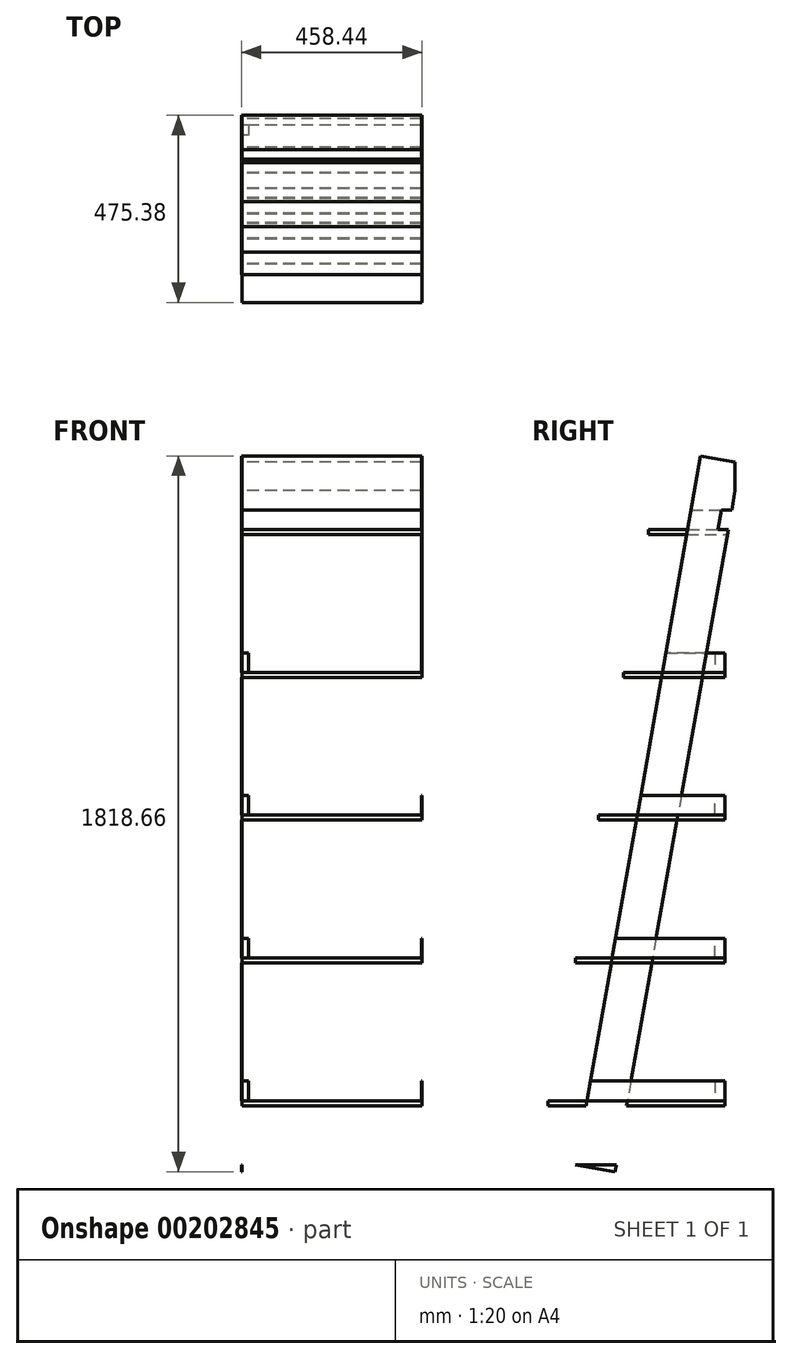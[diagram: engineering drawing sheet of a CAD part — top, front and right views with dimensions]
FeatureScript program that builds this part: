
annotation { "Feature Type Name" : "Feature", "Feature Type Description" : "" }
export const myFeature = defineFeature(function(context is Context, id is Id, definition is map)
    precondition{}
    {
        {
            assignVariable(context, id + "F0", {"name" : "Thickness", "anyValue" : 1.25});
        }
        {
            var Q0;
            Q0=qCreatedBy(makeId("Right.planeOp"),FACE);
            var sketch = newSketch(context, id + "F1", { "sketchPlane" : qUnion([Q0])});
            skLineSegment(sketch, "E0.bottom", {"start": v(317.57, 1801.02) * mm, "end": v(405.12, 1785.58) * mm});
            skLineSegment(sketch, "E0.top", {"start": v(0, 0) * mm, "end": v(100.06, -17.64) * mm});
            skLineSegment(sketch, "E0.left", {"start": v(317.57, 1801.02) * mm, "end": v(0, 0) * mm});
            skLineSegment(sketch, "E0.right", {"start": v(417.62, 1783.37) * mm, "end": v(405.12, 1712.44) * mm, "construction": true});
            skLineSegment(sketch, "E1", {"start": v(405.12, 1712.44) * mm, "end": v(405.12, 1785.58) * mm});
            skLineSegment(sketch, "E2", {"start": v(103.17, 0) * mm, "end": v(0, 0) * mm});
            skLineSegment(sketch, "E3.bottom", {"start": v(26.46, 150.08) * mm, "end": v(129.63, 150.08) * mm});
            skLineSegment(sketch, "E3.top", {"start": v(0, 0) * mm, "end": v(103.17, 0) * mm});
            skLineSegment(sketch, "E3.left", {"start": v(26.46, 150.08) * mm, "end": v(0, 0) * mm});
            skLineSegment(sketch, "E3.right", {"start": v(129.63, 150.08) * mm, "end": v(103.17, 0) * mm});
            skLineSegment(sketch, "E4.bottom", {"start": v(37.5, 212.62) * mm, "end": v(140.66, 212.62) * mm});
            skLineSegment(sketch, "E4.left", {"start": v(37.5, 212.62) * mm, "end": v(26.46, 150.08) * mm});
            skLineSegment(sketch, "E4.right", {"start": v(140.66, 212.62) * mm, "end": v(129.63, 150.08) * mm});
            skLineSegment(sketch, "E5", {"start": v(0, 0) * mm, "end": v(-478.22, 0) * mm, "construction": true});
            skLineSegment(sketch, "E6.0.1.0", {"start": v(204.61, 575.32) * mm, "end": v(193.59, 512.79) * mm});
            skLineSegment(sketch, "E6.0.1.1", {"start": v(101.45, 575.32) * mm, "end": v(204.61, 575.32) * mm});
            skLineSegment(sketch, "E6.0.1.2", {"start": v(101.45, 575.32) * mm, "end": v(90.42, 512.79) * mm});
            skLineSegment(sketch, "E6.0.1.3", {"start": v(90.42, 512.79) * mm, "end": v(193.59, 512.79) * mm});
            skLineSegment(sketch, "E6.0.2.0", {"start": v(268.57, 938.03) * mm, "end": v(257.54, 875.5) * mm});
            skLineSegment(sketch, "E6.0.2.1", {"start": v(165.4, 938.03) * mm, "end": v(268.57, 938.03) * mm});
            skLineSegment(sketch, "E6.0.2.2", {"start": v(165.4, 938.03) * mm, "end": v(154.37, 875.5) * mm});
            skLineSegment(sketch, "E6.0.2.3", {"start": v(154.37, 875.5) * mm, "end": v(257.54, 875.5) * mm});
            skLineSegment(sketch, "E6.0.3.0", {"start": v(332.52, 1300.73) * mm, "end": v(321.5, 1238.2) * mm});
            skLineSegment(sketch, "E6.0.3.1", {"start": v(229.35, 1300.73) * mm, "end": v(332.52, 1300.73) * mm});
            skLineSegment(sketch, "E6.0.3.2", {"start": v(229.35, 1300.73) * mm, "end": v(218.33, 1238.2) * mm});
            skLineSegment(sketch, "E6.0.3.3", {"start": v(218.33, 1238.2) * mm, "end": v(321.5, 1238.2) * mm});
            skLineSegment(sketch, "E6.direction1", {"start": v(129.63, 150.08) * mm, "end": v(405.12, 150.08) * mm, "construction": true});
            skLineSegment(sketch, "E6.direction2", {"start": v(129.63, 150.08) * mm, "end": v(193.59, 512.79) * mm, "construction": true});
            skLineSegment(sketch, "E7.0.0.4", {"start": v(396.48, 1663.44) * mm, "end": v(385.45, 1600.9) * mm});
            skLineSegment(sketch, "E7.3.0.4", {"start": v(293.3, 1663.44) * mm, "end": v(396.48, 1663.44) * mm});
            skLineSegment(sketch, "E7.6.0.4", {"start": v(293.3, 1663.44) * mm, "end": v(282.28, 1600.9) * mm});
            skLineSegment(sketch, "E7.9.0.4", {"start": v(282.28, 1600.9) * mm, "end": v(385.45, 1600.9) * mm});
            skLineSegment(sketch, "E8", {"start": v(405.12, 1785.58) * mm, "end": v(417.62, 1783.37) * mm, "construction": true});
            skLineSegment(sketch, "E9", {"start": v(405.12, 1712.44) * mm, "end": v(100.06, -17.64) * mm});
            skLineSegment(sketch, "E10", {"start": v(405.12, 2231.58) * mm, "end": v(405.12, 0) * mm, "construction": true});
            skPoint(sketch, "E11.firstSnap0", {"position": v(267.37, 150.08) * mm});
            skLineSegment(sketch, "E11.bottom", {"start": v(-70.26, 150.08) * mm, "end": v(379.72, 150.08) * mm});
            skLineSegment(sketch, "E11.top", {"start": v(-70.26, 162.78) * mm, "end": v(379.72, 162.78) * mm});
            skLineSegment(sketch, "E11.left", {"start": v(-70.26, 150.08) * mm, "end": v(-70.26, 162.78) * mm});
            skLineSegment(sketch, "E11.right", {"start": v(379.72, 150.08) * mm, "end": v(379.72, 162.78) * mm});
            skLineSegment(sketch, "E12.bottom", {"start": v(185.56, 1613.6) * mm, "end": v(387.69, 1613.6) * mm});
            skLineSegment(sketch, "E12.top", {"start": v(185.56, 1600.9) * mm, "end": v(387.69, 1600.9) * mm});
            skLineSegment(sketch, "E12.left", {"start": v(185.56, 1613.6) * mm, "end": v(185.56, 1600.9) * mm});
            skLineSegment(sketch, "E12.right", {"start": v(387.69, 1613.6) * mm, "end": v(387.69, 1600.9) * mm});
            skLineSegment(sketch, "E13.bottom", {"start": v(379.72, 1250.9) * mm, "end": v(121.6, 1250.9) * mm});
            skLineSegment(sketch, "E13.top", {"start": v(379.72, 1238.2) * mm, "end": v(121.6, 1238.2) * mm});
            skLineSegment(sketch, "E13.left", {"start": v(379.72, 1250.9) * mm, "end": v(379.72, 1238.2) * mm});
            skLineSegment(sketch, "E13.right", {"start": v(121.6, 1250.9) * mm, "end": v(121.6, 1238.2) * mm});
            skLineSegment(sketch, "E14.bottom", {"start": v(379.72, 888.2) * mm, "end": v(57.65, 888.2) * mm});
            skLineSegment(sketch, "E14.top", {"start": v(379.72, 875.5) * mm, "end": v(57.65, 875.5) * mm});
            skLineSegment(sketch, "E14.left", {"start": v(379.72, 888.2) * mm, "end": v(379.72, 875.5) * mm});
            skLineSegment(sketch, "E14.right", {"start": v(57.65, 888.2) * mm, "end": v(57.65, 875.5) * mm});
            skLineSegment(sketch, "E15.bottom", {"start": v(379.72, 512.79) * mm, "end": v(0, 512.79) * mm});
            skLineSegment(sketch, "E15.top", {"start": v(379.72, 525.49) * mm, "end": v(0, 525.49) * mm});
            skLineSegment(sketch, "E15.left", {"start": v(379.72, 525.49) * mm, "end": v(379.72, 512.79) * mm});
            skLineSegment(sketch, "E15.right", {"start": v(0, 525.49) * mm, "end": v(0, 512.79) * mm});
            skLineSegment(sketch, "E16", {"start": v(247.42, 1951.7) * mm, "end": v(-87, 55.12) * mm, "construction": true});
            skLineSegment(sketch, "E17", {"start": v(396.48, 1663.44) * mm, "end": v(387.69, 1613.6) * mm});
            skLineSegment(sketch, "E18", {"start": v(361.9, 1613.6) * mm, "end": v(370.68, 1663.44) * mm});
            skLineSegment(sketch, "E19", {"start": v(379.72, 1250.9) * mm, "end": v(379.72, 1300.73) * mm});
            skLineSegment(sketch, "E20", {"start": v(379.72, 1300.73) * mm, "end": v(332.52, 1300.73) * mm});
            skLineSegment(sketch, "E21", {"start": v(354.32, 1300.73) * mm, "end": v(354.32, 1250.9) * mm});
            skLineSegment(sketch, "E22", {"start": v(379.72, 888.2) * mm, "end": v(379.72, 938.03) * mm});
            skLineSegment(sketch, "E23", {"start": v(379.72, 938.03) * mm, "end": v(268.57, 938.03) * mm});
            skLineSegment(sketch, "E24", {"start": v(379.72, 525.49) * mm, "end": v(379.72, 575.32) * mm});
            skLineSegment(sketch, "E25", {"start": v(379.72, 575.32) * mm, "end": v(204.61, 575.32) * mm});
            skLineSegment(sketch, "E26", {"start": v(379.72, 162.78) * mm, "end": v(379.72, 212.62) * mm});
            skLineSegment(sketch, "E27", {"start": v(379.72, 212.62) * mm, "end": v(140.66, 212.62) * mm});
            skLineSegment(sketch, "E28", {"start": v(354.32, 212.62) * mm, "end": v(354.32, 162.78) * mm});
            skLineSegment(sketch, "E29", {"start": v(354.32, 525.49) * mm, "end": v(354.32, 575.32) * mm});
            skLineSegment(sketch, "E30", {"start": v(354.32, 888.2) * mm, "end": v(354.32, 938.03) * mm});
            skSolve(sketch);
        }
        {
            var Q0;
            {var subQ4=sQuery(id+"F1.wireOp",EDGE,"E0.bottom");Q0=makeQuery(id+"F1.imprint","IMPRINT",FACE,{"disambiguationData":[TD([[makeQuery(id+"F1.imprint","IMPRINT",EDGE,{"derivedFrom":subQ4}),-1.0]])]});}
            var Q1;
            {var subQ0=sQuery(id+"F1.wireOp",EDGE,"E17");Q1=makeQuery(id+"F1.imprint","IMPRINT",FACE,{"disambiguationData":[TD([[makeQuery(id+"F1.imprint","IMPRINT",EDGE,{"derivedFrom":subQ0}),-1.0]])]});}
            var Q2;
            {var subQ3=sQuery(id+"F1.wireOp",EDGE,"E18");Q2=makeQuery(id+"F1.imprint","IMPRINT",FACE,{"disambiguationData":[TD([[makeQuery(id+"F1.imprint","IMPRINT",EDGE,{"derivedFrom":subQ3}),1.0]])]});}
            var Q3;
            {var subQ0=sQuery(id+"F1.wireOp",EDGE,"E12.bottom");var subQ3=makeQuery(id+"F1.imprint","INTERSECT",VERTEX,{"derivedFrom":[subQ0,sQuery(id+"F1.wireOp",EDGE,"E18")]});Q3=makeQuery(id+"F1.imprint","IMPRINT",FACE,{"disambiguationData":[TD([[makeQuery(id+"F1.imprint","IMPRINT",EDGE,{"disambiguationData":[TD([[subQ3,1.0]])],"derivedFrom":subQ0}),-1.0]])]});}
            var Q4;
            {var subQ0=sQuery(id+"F1.wireOp",EDGE,"E6.0.3.1");Q4=makeQuery(id+"F1.imprint","IMPRINT",FACE,{"disambiguationData":[TD([[makeQuery(id+"F1.imprint","IMPRINT",EDGE,{"derivedFrom":subQ0}),1.0]])]});}
            var Q5;
            {var subQ0=sQuery(id+"F1.wireOp",EDGE,"E6.0.3.1");Q5=makeQuery(id+"F1.imprint","IMPRINT",FACE,{"disambiguationData":[TD([[makeQuery(id+"F1.imprint","IMPRINT",EDGE,{"derivedFrom":subQ0}),-1.0]])]});}
            var Q6;
            {var subQ0=sQuery(id+"F1.wireOp",EDGE,"E13.top");var subQ5=sQuery(id+"F1.wireOp",EDGE,"E9");var subQ6=makeQuery(id+"F1.imprint","INTERSECT",VERTEX,{"derivedFrom":[subQ5,subQ0]});Q6=makeQuery(id+"F1.imprint","IMPRINT",FACE,{"disambiguationData":[TD([[makeQuery(id+"F1.imprint","IMPRINT",EDGE,{"disambiguationData":[TD([[subQ6,1.0]])],"derivedFrom":subQ5}),-1.0]])]});}
            var Q7;
            {var subQ0=sQuery(id+"F1.wireOp",EDGE,"E6.0.2.1");Q7=makeQuery(id+"F1.imprint","IMPRINT",FACE,{"disambiguationData":[TD([[makeQuery(id+"F1.imprint","IMPRINT",EDGE,{"derivedFrom":subQ0}),1.0]])]});}
            var Q8;
            {var subQ0=sQuery(id+"F1.wireOp",EDGE,"E6.0.2.1");Q8=makeQuery(id+"F1.imprint","IMPRINT",FACE,{"disambiguationData":[TD([[makeQuery(id+"F1.imprint","IMPRINT",EDGE,{"derivedFrom":subQ0}),-1.0]])]});}
            var Q9;
            {var subQ0=sQuery(id+"F1.wireOp",EDGE,"E6.0.1.1");Q9=makeQuery(id+"F1.imprint","IMPRINT",FACE,{"disambiguationData":[TD([[makeQuery(id+"F1.imprint","IMPRINT",EDGE,{"derivedFrom":subQ0}),1.0]])]});}
            var Q10;
            {var subQ0=sQuery(id+"F1.wireOp",EDGE,"E14.top");var subQ5=sQuery(id+"F1.wireOp",EDGE,"E9");var subQ6=makeQuery(id+"F1.imprint","INTERSECT",VERTEX,{"derivedFrom":[subQ5,subQ0]});Q10=makeQuery(id+"F1.imprint","IMPRINT",FACE,{"disambiguationData":[TD([[makeQuery(id+"F1.imprint","IMPRINT",EDGE,{"disambiguationData":[TD([[subQ6,1.0]])],"derivedFrom":subQ5}),-1.0]])]});}
            var Q11;
            {var subQ0=sQuery(id+"F1.wireOp",EDGE,"E6.0.1.1");Q11=makeQuery(id+"F1.imprint","IMPRINT",FACE,{"disambiguationData":[TD([[makeQuery(id+"F1.imprint","IMPRINT",EDGE,{"derivedFrom":subQ0}),-1.0]])]});}
            var Q12;
            {var subQ0=sQuery(id+"F1.wireOp",EDGE,"E15.bottom");var subQ5=sQuery(id+"F1.wireOp",EDGE,"E9");var subQ6=makeQuery(id+"F1.imprint","INTERSECT",VERTEX,{"derivedFrom":[subQ5,subQ0]});Q12=makeQuery(id+"F1.imprint","IMPRINT",FACE,{"disambiguationData":[TD([[makeQuery(id+"F1.imprint","IMPRINT",EDGE,{"disambiguationData":[TD([[subQ6,1.0]])],"derivedFrom":subQ5}),-1.0]])]});}
            var Q13;
            {var subQ0=sQuery(id+"F1.wireOp",EDGE,"E4.bottom");Q13=makeQuery(id+"F1.imprint","IMPRINT",FACE,{"disambiguationData":[TD([[makeQuery(id+"F1.imprint","IMPRINT",EDGE,{"derivedFrom":subQ0}),1.0]])]});}
            var Q14;
            {var subQ0=sQuery(id+"F1.wireOp",EDGE,"E4.bottom");Q14=makeQuery(id+"F1.imprint","IMPRINT",FACE,{"disambiguationData":[TD([[makeQuery(id+"F1.imprint","IMPRINT",EDGE,{"derivedFrom":subQ0}),-1.0]])]});}
            var Q15;
            {var subQ0=sQuery(id+"F1.wireOp",EDGE,"E11.bottom");var subQ5=sQuery(id+"F1.wireOp",EDGE,"E9");var subQ6=makeQuery(id+"F1.imprint","INTERSECT",VERTEX,{"derivedFrom":[subQ5,subQ0]});Q15=makeQuery(id+"F1.imprint","IMPRINT",FACE,{"disambiguationData":[TD([[makeQuery(id+"F1.imprint","IMPRINT",EDGE,{"disambiguationData":[TD([[subQ6,1.0]])],"derivedFrom":subQ5}),-1.0]])]});}
            var Q16;
            {var subQ0=sQuery(id+"F1.wireOp",EDGE,"E3.top");Q16=makeQuery(id+"F1.imprint","IMPRINT",FACE,{"disambiguationData":[TD([[makeQuery(id+"F1.imprint","IMPRINT",EDGE,{"derivedFrom":subQ0}),1.0]])]});}
            extrude(context, id + "F2", {"entities" : qUnion([Q0, Q1, Q2, Q3, Q4, Q5, Q6, Q7, Q8, Q9, Q10, Q11, Q12, Q13, Q14, Q15, Q16]), "oppositeDirection" : true, "depth" : (getVariable(context, 'Thickness') / 2) * mm});
        }
        {
            var Q0;
            {var subQ4=sQuery(id+"F1.wireOp",EDGE,"E0.bottom");Q0=makeQuery(id+"F1.imprint","IMPRINT",FACE,{"disambiguationData":[TD([[makeQuery(id+"F1.imprint","IMPRINT",EDGE,{"derivedFrom":subQ4}),-1.0]])]});}
            var Q1;
            {var subQ0=sQuery(id+"F1.wireOp",EDGE,"E6.0.3.1");Q1=makeQuery(id+"F1.imprint","IMPRINT",FACE,{"disambiguationData":[TD([[makeQuery(id+"F1.imprint","IMPRINT",EDGE,{"derivedFrom":subQ0}),1.0]])]});}
            var Q2;
            {var subQ0=sQuery(id+"F1.wireOp",EDGE,"E6.0.2.1");Q2=makeQuery(id+"F1.imprint","IMPRINT",FACE,{"disambiguationData":[TD([[makeQuery(id+"F1.imprint","IMPRINT",EDGE,{"derivedFrom":subQ0}),1.0]])]});}
            var Q3;
            {var subQ0=sQuery(id+"F1.wireOp",EDGE,"E6.0.1.1");Q3=makeQuery(id+"F1.imprint","IMPRINT",FACE,{"disambiguationData":[TD([[makeQuery(id+"F1.imprint","IMPRINT",EDGE,{"derivedFrom":subQ0}),1.0]])]});}
            var Q4;
            {var subQ0=sQuery(id+"F1.wireOp",EDGE,"E4.bottom");Q4=makeQuery(id+"F1.imprint","IMPRINT",FACE,{"disambiguationData":[TD([[makeQuery(id+"F1.imprint","IMPRINT",EDGE,{"derivedFrom":subQ0}),1.0]])]});}
            var Q5;
            {var subQ0=sQuery(id+"F1.wireOp",EDGE,"E3.top");Q5=makeQuery(id+"F1.imprint","IMPRINT",FACE,{"disambiguationData":[TD([[makeQuery(id+"F1.imprint","IMPRINT",EDGE,{"derivedFrom":subQ0}),1.0]])]});}
            extrude(context, id + "F3", {"entities" : qUnion([Q0, Q1, Q2, Q3, Q4, Q5]), "operationType" : NewBodyOperationType.ADD, "depth" : (getVariable(context, 'Thickness') / 2) * mm});
        }
        {
            var Q0;
            {var subQ5=sQuery(id+"F1.wireOp",EDGE,"E11.right");Q0=makeQuery(id+"F1.imprint","IMPRINT",FACE,{"disambiguationData":[TD([[makeQuery(id+"F1.imprint","IMPRINT",EDGE,{"derivedFrom":subQ5}),1.0]])]});}
            var Q1;
            {var subQ5=sQuery(id+"F1.wireOp",EDGE,"E11.left");Q1=makeQuery(id+"F1.imprint","IMPRINT",FACE,{"disambiguationData":[TD([[makeQuery(id+"F1.imprint","IMPRINT",EDGE,{"derivedFrom":subQ5}),-1.0]])]});}
            var Q2;
            {var subQ3=sQuery(id+"F1.wireOp",EDGE,"E11.top");var subQ5=sQuery(id+"F1.wireOp",EDGE,"E9");var subQ7=makeQuery(id+"F1.imprint","INTERSECT",VERTEX,{"derivedFrom":[subQ5,subQ3]});Q2=makeQuery(id+"F1.imprint","IMPRINT",FACE,{"disambiguationData":[TD([[makeQuery(id+"F1.imprint","IMPRINT",EDGE,{"disambiguationData":[TD([[subQ7,-1.0]])],"derivedFrom":subQ5}),-1.0]])]});}
            var Q3;
            {var subQ5=sQuery(id+"F1.wireOp",EDGE,"E15.right");Q3=makeQuery(id+"F1.imprint","IMPRINT",FACE,{"disambiguationData":[TD([[makeQuery(id+"F1.imprint","IMPRINT",EDGE,{"derivedFrom":subQ5}),1.0]])]});}
            var Q4;
            {var subQ3=sQuery(id+"F1.wireOp",EDGE,"E15.top");var subQ5=sQuery(id+"F1.wireOp",EDGE,"E9");var subQ7=makeQuery(id+"F1.imprint","INTERSECT",VERTEX,{"derivedFrom":[subQ5,subQ3]});Q4=makeQuery(id+"F1.imprint","IMPRINT",FACE,{"disambiguationData":[TD([[makeQuery(id+"F1.imprint","IMPRINT",EDGE,{"disambiguationData":[TD([[subQ7,-1.0]])],"derivedFrom":subQ5}),-1.0]])]});}
            var Q5;
            {var subQ5=sQuery(id+"F1.wireOp",EDGE,"E15.left");Q5=makeQuery(id+"F1.imprint","IMPRINT",FACE,{"disambiguationData":[TD([[makeQuery(id+"F1.imprint","IMPRINT",EDGE,{"derivedFrom":subQ5}),-1.0]])]});}
            var Q6;
            {var subQ5=sQuery(id+"F1.wireOp",EDGE,"E14.right");Q6=makeQuery(id+"F1.imprint","IMPRINT",FACE,{"disambiguationData":[TD([[makeQuery(id+"F1.imprint","IMPRINT",EDGE,{"derivedFrom":subQ5}),1.0]])]});}
            var Q7;
            {var subQ3=sQuery(id+"F1.wireOp",EDGE,"E14.bottom");var subQ5=sQuery(id+"F1.wireOp",EDGE,"E9");var subQ6=makeQuery(id+"F1.imprint","INTERSECT",VERTEX,{"derivedFrom":[subQ5,subQ3]});Q7=makeQuery(id+"F1.imprint","IMPRINT",FACE,{"disambiguationData":[TD([[makeQuery(id+"F1.imprint","IMPRINT",EDGE,{"disambiguationData":[TD([[subQ6,-1.0]])],"derivedFrom":subQ5}),-1.0]])]});}
            var Q8;
            {var subQ5=sQuery(id+"F1.wireOp",EDGE,"E14.left");Q8=makeQuery(id+"F1.imprint","IMPRINT",FACE,{"disambiguationData":[TD([[makeQuery(id+"F1.imprint","IMPRINT",EDGE,{"derivedFrom":subQ5}),-1.0]])]});}
            var Q9;
            {var subQ5=sQuery(id+"F1.wireOp",EDGE,"E13.right");Q9=makeQuery(id+"F1.imprint","IMPRINT",FACE,{"disambiguationData":[TD([[makeQuery(id+"F1.imprint","IMPRINT",EDGE,{"derivedFrom":subQ5}),1.0]])]});}
            var Q10;
            {var subQ3=sQuery(id+"F1.wireOp",EDGE,"E13.bottom");var subQ5=sQuery(id+"F1.wireOp",EDGE,"E9");var subQ6=makeQuery(id+"F1.imprint","INTERSECT",VERTEX,{"derivedFrom":[subQ5,subQ3]});Q10=makeQuery(id+"F1.imprint","IMPRINT",FACE,{"disambiguationData":[TD([[makeQuery(id+"F1.imprint","IMPRINT",EDGE,{"disambiguationData":[TD([[subQ6,-1.0]])],"derivedFrom":subQ5}),-1.0]])]});}
            var Q11;
            {var subQ5=sQuery(id+"F1.wireOp",EDGE,"E13.left");Q11=makeQuery(id+"F1.imprint","IMPRINT",FACE,{"disambiguationData":[TD([[makeQuery(id+"F1.imprint","IMPRINT",EDGE,{"derivedFrom":subQ5}),-1.0]])]});}
            var Q12;
            {var subQ5=sQuery(id+"F1.wireOp",EDGE,"E12.left");Q12=makeQuery(id+"F1.imprint","IMPRINT",FACE,{"disambiguationData":[TD([[makeQuery(id+"F1.imprint","IMPRINT",EDGE,{"derivedFrom":subQ5}),1.0]])]});}
            var Q13;
            {var subQ1=sQuery(id+"F1.wireOp",EDGE,"E7.6.0.4");var subQ3=sQuery(id+"F1.wireOp",EDGE,"E12.bottom");var subQ4=makeQuery(id+"F1.imprint","INTERSECT",VERTEX,{"derivedFrom":[subQ1,subQ3]});Q13=makeQuery(id+"F1.imprint","IMPRINT",FACE,{"disambiguationData":[TD([[makeQuery(id+"F1.imprint","IMPRINT",EDGE,{"disambiguationData":[TD([[subQ4,-1.0]])],"derivedFrom":subQ1}),1.0]])]});}
            extrude(context, id + "F4", {"entities" : qUnion([Q0, Q1, Q2, Q3, Q4, Q5, Q6, Q7, Q8, Q9, Q10, Q11, Q12, Q13]), "depth" : 457.2 * mm});
        }
        {
            var Q0;
            {var subQ5=sQuery(id+"F1.wireOp",EDGE,"E28");Q0=makeQuery(id+"F1.imprint","IMPRINT",FACE,{"disambiguationData":[TD([[makeQuery(id+"F1.imprint","IMPRINT",EDGE,{"derivedFrom":subQ5}),-1.0]])]});}
            var Q1;
            {var subQ0=sQuery(id+"F1.wireOp",EDGE,"E4.bottom");Q1=makeQuery(id+"F1.imprint","IMPRINT",FACE,{"disambiguationData":[TD([[makeQuery(id+"F1.imprint","IMPRINT",EDGE,{"derivedFrom":subQ0}),-1.0]])]});}
            var Q2;
            {var subQ0=sQuery(id+"F1.wireOp",EDGE,"E26");Q2=makeQuery(id+"F1.imprint","IMPRINT",FACE,{"disambiguationData":[TD([[makeQuery(id+"F1.imprint","IMPRINT",EDGE,{"derivedFrom":subQ0}),1.0]])]});}
            var Q3;
            {var subQ0=sQuery(id+"F1.wireOp",EDGE,"E6.0.1.1");Q3=makeQuery(id+"F1.imprint","IMPRINT",FACE,{"disambiguationData":[TD([[makeQuery(id+"F1.imprint","IMPRINT",EDGE,{"derivedFrom":subQ0}),-1.0]])]});}
            var Q4;
            {var subQ5=sQuery(id+"F1.wireOp",EDGE,"E29");Q4=makeQuery(id+"F1.imprint","IMPRINT",FACE,{"disambiguationData":[TD([[makeQuery(id+"F1.imprint","IMPRINT",EDGE,{"derivedFrom":subQ5}),1.0]])]});}
            var Q5;
            {var subQ0=sQuery(id+"F1.wireOp",EDGE,"E24");Q5=makeQuery(id+"F1.imprint","IMPRINT",FACE,{"disambiguationData":[TD([[makeQuery(id+"F1.imprint","IMPRINT",EDGE,{"derivedFrom":subQ0}),1.0]])]});}
            var Q6;
            {var subQ0=sQuery(id+"F1.wireOp",EDGE,"E6.0.2.1");Q6=makeQuery(id+"F1.imprint","IMPRINT",FACE,{"disambiguationData":[TD([[makeQuery(id+"F1.imprint","IMPRINT",EDGE,{"derivedFrom":subQ0}),-1.0]])]});}
            var Q7;
            {var subQ5=sQuery(id+"F1.wireOp",EDGE,"E30");Q7=makeQuery(id+"F1.imprint","IMPRINT",FACE,{"disambiguationData":[TD([[makeQuery(id+"F1.imprint","IMPRINT",EDGE,{"derivedFrom":subQ5}),1.0]])]});}
            var Q8;
            {var subQ0=sQuery(id+"F1.wireOp",EDGE,"E22");Q8=makeQuery(id+"F1.imprint","IMPRINT",FACE,{"disambiguationData":[TD([[makeQuery(id+"F1.imprint","IMPRINT",EDGE,{"derivedFrom":subQ0}),1.0]])]});}
            var Q9;
            {var subQ0=sQuery(id+"F1.wireOp",EDGE,"E19");Q9=makeQuery(id+"F1.imprint","IMPRINT",FACE,{"disambiguationData":[TD([[makeQuery(id+"F1.imprint","IMPRINT",EDGE,{"derivedFrom":subQ0}),1.0]])]});}
            var Q10;
            {var subQ5=sQuery(id+"F1.wireOp",EDGE,"E21");Q10=makeQuery(id+"F1.imprint","IMPRINT",FACE,{"disambiguationData":[TD([[makeQuery(id+"F1.imprint","IMPRINT",EDGE,{"derivedFrom":subQ5}),-1.0]])]});}
            var Q11;
            {var subQ0=sQuery(id+"F1.wireOp",EDGE,"E6.0.3.1");Q11=makeQuery(id+"F1.imprint","IMPRINT",FACE,{"disambiguationData":[TD([[makeQuery(id+"F1.imprint","IMPRINT",EDGE,{"derivedFrom":subQ0}),-1.0]])]});}
            var Q12;
            {var subQ3=sQuery(id+"F1.wireOp",EDGE,"E18");Q12=makeQuery(id+"F1.imprint","IMPRINT",FACE,{"disambiguationData":[TD([[makeQuery(id+"F1.imprint","IMPRINT",EDGE,{"derivedFrom":subQ3}),1.0]])]});}
            var Q13;
            {var subQ0=sQuery(id+"F1.wireOp",EDGE,"E17");Q13=makeQuery(id+"F1.imprint","IMPRINT",FACE,{"disambiguationData":[TD([[makeQuery(id+"F1.imprint","IMPRINT",EDGE,{"derivedFrom":subQ0}),-1.0]])]});}
            extrude(context, id + "F5", {"entities" : qUnion([Q0, Q1, Q2, Q3, Q4, Q5, Q6, Q7, Q8, Q9, Q10, Q11, Q12, Q13]), "depth" : (getVariable(context, 'Thickness') / 2) * mm});
        }
        {
            var Q0;
            {var subQ0=sQuery(id+"F1.wireOp",EDGE,"E26");Q0=makeQuery(id+"F1.imprint","IMPRINT",FACE,{"disambiguationData":[TD([[makeQuery(id+"F1.imprint","IMPRINT",EDGE,{"derivedFrom":subQ0}),1.0]])]});}
            var Q1;
            {var subQ0=sQuery(id+"F1.wireOp",EDGE,"E24");Q1=makeQuery(id+"F1.imprint","IMPRINT",FACE,{"disambiguationData":[TD([[makeQuery(id+"F1.imprint","IMPRINT",EDGE,{"derivedFrom":subQ0}),1.0]])]});}
            var Q2;
            {var subQ0=sQuery(id+"F1.wireOp",EDGE,"E22");Q2=makeQuery(id+"F1.imprint","IMPRINT",FACE,{"disambiguationData":[TD([[makeQuery(id+"F1.imprint","IMPRINT",EDGE,{"derivedFrom":subQ0}),1.0]])]});}
            var Q3;
            {var subQ0=sQuery(id+"F1.wireOp",EDGE,"E19");Q3=makeQuery(id+"F1.imprint","IMPRINT",FACE,{"disambiguationData":[TD([[makeQuery(id+"F1.imprint","IMPRINT",EDGE,{"derivedFrom":subQ0}),1.0]])]});}
            var Q4;
            {var subQ0=sQuery(id+"F1.wireOp",EDGE,"E17");Q4=makeQuery(id+"F1.imprint","IMPRINT",FACE,{"disambiguationData":[TD([[makeQuery(id+"F1.imprint","IMPRINT",EDGE,{"derivedFrom":subQ0}),-1.0]])]});}
            extrude(context, id + "F6", {"entities" : qUnion([Q0, Q1, Q2, Q3, Q4]), "depth" : (18 - (getVariable(context, 'Thickness') / 2)) * mm, "hasSecondDirection" : true, "secondDirectionOppositeDirection" : false, "secondDirectionDepth" : (getVariable(context, 'Thickness') / 2) * mm});
        }
        {
            var Q0;
            Q0=qCreatedBy(makeId("Top.planeOp"),FACE);
            var sketch = newSketch(context, id + "F7", { "sketchPlane" : qUnion([Q0])});
            skLineSegment(sketch, "E31", {"start": v(228.6, -131.68) * mm, "end": v(228.6, 85) * mm});
            skSolve(sketch);
        }
        {
            var Q0;
            Q0=sQuery(id+"F7.wireOp",EDGE,"E31");
            extrude(context, id + "F8", {"bodyType" : ToolBodyType.SURFACE, "surfaceEntities" : qUnion([Q0]), "depth" : 2171.52 * mm});
        }
        {
            var Q0;
            Q0=sQuery(id+"F7.wireOp",EDGE,"E31");
            extrude(context, id + "F9", {"bodyType" : ToolBodyType.SURFACE, "surfaceEntities" : qUnion([Q0]), "depth" : 50.8 * mm});
        }
        {
            var Q0;
            Q0=makeQuery(id+"F2.opExtrude","SWEPT_BODY",BODY,{"disambiguationData":[OSD([sQuery(id+"F1.wireOp",EDGE,"E0.bottom"),sQuery(id+"F1.wireOp",EDGE,"E0.left"),sQuery(id+"F1.wireOp",EDGE,"E1"),sQuery(id+"F1.wireOp",EDGE,"E3.top"),sQuery(id+"F1.wireOp",EDGE,"E3.left"),sQuery(id+"F1.wireOp",EDGE,"E4.left"),sQuery(id+"F1.wireOp",EDGE,"E6.0.1.2"),sQuery(id+"F1.wireOp",EDGE,"E6.0.2.2"),sQuery(id+"F1.wireOp",EDGE,"E6.0.3.2"),sQuery(id+"F1.wireOp",EDGE,"E7.6.0.4"),sQuery(id+"F1.wireOp",EDGE,"E9"),sQuery(id+"F1.wireOp",EDGE,"E17")])]});
            var Q1;
            Q1=makeQuery(id+"F9.opExtrude","SWEPT_FACE",FACE,{"disambiguationData":[OSD([sQuery(id+"F7.wireOp",EDGE,"E31")])]});
            mirror(context, id + "F10", {"entities" : qUnion([Q0]), "mirrorPlane" : qUnion([Q1])});
        }
        {
            var Q0;
            Q0=makeQuery(id+"FsbkJnUSSRytLsG_1.opExtrude","SWEPT_BODY",BODY,{"disambiguationData":[OSD([sQuery(id+"F1.wireOp",EDGE,"E3.top"),sQuery(id+"F1.wireOp",EDGE,"E3.left"),sQuery(id+"F1.wireOp",EDGE,"E9"),sQuery(id+"F1.wireOp",EDGE,"E11.bottom")])]});
            var Q1;
            Q1=makeQuery(id+"F5.opExtrude","SWEPT_BODY",BODY,{"disambiguationData":[OSD([sQuery(id+"F1.wireOp",EDGE,"E4.bottom"),sQuery(id+"F1.wireOp",EDGE,"E4.left"),sQuery(id+"F1.wireOp",EDGE,"E11.top"),sQuery(id+"F1.wireOp",EDGE,"E26"),sQuery(id+"F1.wireOp",EDGE,"E27")])]});
            var Q2;
            Q2=makeQuery(id+"FsbkJnUSSRytLsG_1.opExtrude","SWEPT_BODY",BODY,{"disambiguationData":[OSD([sQuery(id+"F1.wireOp",EDGE,"E0.left"),sQuery(id+"F1.wireOp",EDGE,"E4.bottom"),sQuery(id+"F1.wireOp",EDGE,"E9"),sQuery(id+"F1.wireOp",EDGE,"E15.bottom")])]});
            var Q3;
            Q3=makeQuery(id+"F5.opExtrude","SWEPT_BODY",BODY,{"disambiguationData":[OSD([sQuery(id+"F1.wireOp",EDGE,"E6.0.1.1"),sQuery(id+"F1.wireOp",EDGE,"E6.0.1.2"),sQuery(id+"F1.wireOp",EDGE,"E15.top"),sQuery(id+"F1.wireOp",EDGE,"E24"),sQuery(id+"F1.wireOp",EDGE,"E25")])]});
            var Q4;
            Q4=makeQuery(id+"FsbkJnUSSRytLsG_1.opExtrude","SWEPT_BODY",BODY,{"disambiguationData":[OSD([sQuery(id+"F1.wireOp",EDGE,"E0.left"),sQuery(id+"F1.wireOp",EDGE,"E6.0.1.1"),sQuery(id+"F1.wireOp",EDGE,"E9"),sQuery(id+"F1.wireOp",EDGE,"E14.top")])]});
            var Q5;
            Q5=makeQuery(id+"F5.opExtrude","SWEPT_BODY",BODY,{"disambiguationData":[OSD([sQuery(id+"F1.wireOp",EDGE,"E6.0.2.1"),sQuery(id+"F1.wireOp",EDGE,"E6.0.2.2"),sQuery(id+"F1.wireOp",EDGE,"E14.bottom"),sQuery(id+"F1.wireOp",EDGE,"E22"),sQuery(id+"F1.wireOp",EDGE,"E23")])]});
            var Q6;
            Q6=makeQuery(id+"FsbkJnUSSRytLsG_1.opExtrude","SWEPT_BODY",BODY,{"disambiguationData":[OSD([sQuery(id+"F1.wireOp",EDGE,"E0.left"),sQuery(id+"F1.wireOp",EDGE,"E6.0.2.1"),sQuery(id+"F1.wireOp",EDGE,"E9"),sQuery(id+"F1.wireOp",EDGE,"E13.top")])]});
            var Q7;
            Q7=makeQuery(id+"F5.opExtrude","SWEPT_BODY",BODY,{"disambiguationData":[OSD([sQuery(id+"F1.wireOp",EDGE,"E6.0.3.1"),sQuery(id+"F1.wireOp",EDGE,"E6.0.3.2"),sQuery(id+"F1.wireOp",EDGE,"E13.bottom"),sQuery(id+"F1.wireOp",EDGE,"E19"),sQuery(id+"F1.wireOp",EDGE,"E20")])]});
            var Q8;
            Q8=makeQuery(id+"FsbkJnUSSRytLsG_1.opExtrude","SWEPT_BODY",BODY,{"disambiguationData":[OSD([sQuery(id+"F1.wireOp",EDGE,"E0.left"),sQuery(id+"F1.wireOp",EDGE,"E6.0.3.1"),sQuery(id+"F1.wireOp",EDGE,"E9"),sQuery(id+"F1.wireOp",EDGE,"E12.top")])]});
            var Q9;
            Q9=makeQuery(id+"F5.opExtrude","SWEPT_BODY",BODY,{"disambiguationData":[OSD([sQuery(id+"F1.wireOp",EDGE,"E7.3.0.4"),sQuery(id+"F1.wireOp",EDGE,"E7.6.0.4"),sQuery(id+"F1.wireOp",EDGE,"E12.bottom"),sQuery(id+"F1.wireOp",EDGE,"E17")])]});
            var Q10;
            Q10=makeQuery(id+"FsbkJnUSSRytLsG_1.opExtrude","SWEPT_BODY",BODY,{"disambiguationData":[OSD([sQuery(id+"F1.wireOp",EDGE,"E0.bottom"),sQuery(id+"F1.wireOp",EDGE,"E0.left"),sQuery(id+"F1.wireOp",EDGE,"E1"),sQuery(id+"F1.wireOp",EDGE,"E7.3.0.4"),sQuery(id+"F1.wireOp",EDGE,"E9")])]});
            var Q11;
            Q11=makeQuery(id+"FjGixuGb5bzn5mA_0.opExtrude","SWEPT_BODY",BODY,{"disambiguationData":[OSD([sQuery(id+"F1.wireOp",EDGE,"E0.bottom"),sQuery(id+"F1.wireOp",EDGE,"E0.left"),sQuery(id+"F1.wireOp",EDGE,"E1"),sQuery(id+"F1.wireOp",EDGE,"E3.top"),sQuery(id+"F1.wireOp",EDGE,"E3.left"),sQuery(id+"F1.wireOp",EDGE,"E4.left"),sQuery(id+"F1.wireOp",EDGE,"E6.0.1.2"),sQuery(id+"F1.wireOp",EDGE,"E6.0.2.2"),sQuery(id+"F1.wireOp",EDGE,"E6.0.3.2"),sQuery(id+"F1.wireOp",EDGE,"E7.6.0.4"),sQuery(id+"F1.wireOp",EDGE,"E9"),sQuery(id+"F1.wireOp",EDGE,"E17")])]});
            var Q12;
            Q12=makeQuery(id+"F8.opExtrude","SWEPT_FACE",FACE,{"disambiguationData":[OSD([sQuery(id+"F7.wireOp",EDGE,"E31")])]});
            mirror(context, id + "F11", {"entities" : qUnion([Q0, Q1, Q2, Q3, Q4, Q5, Q6, Q7, Q8, Q9, Q10, Q11]), "mirrorPlane" : qUnion([Q12])});
        }
    });
